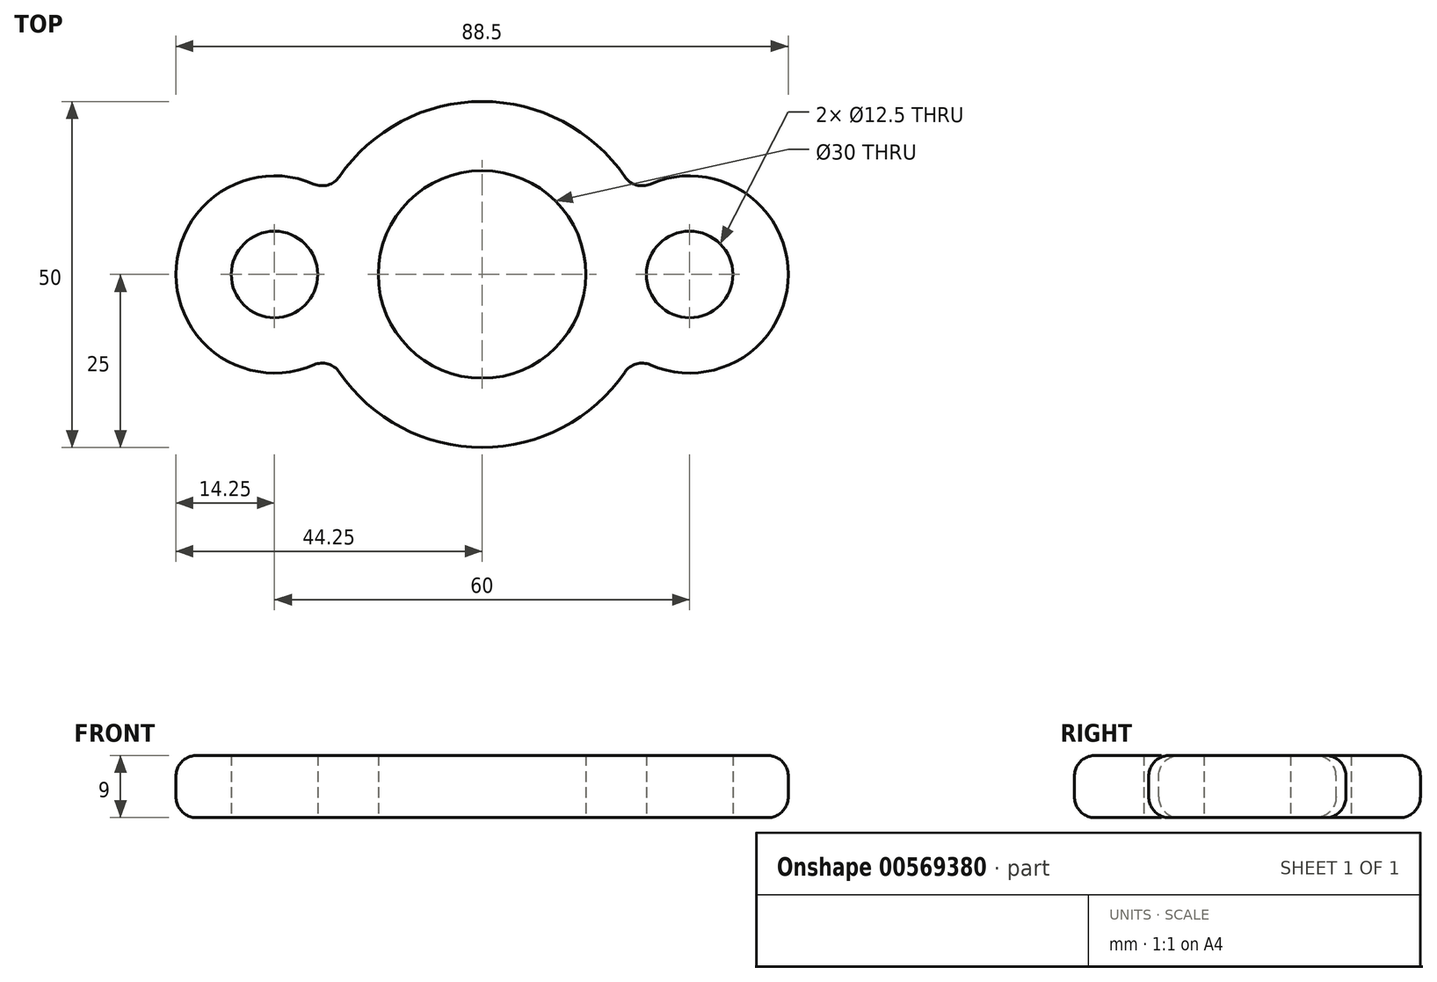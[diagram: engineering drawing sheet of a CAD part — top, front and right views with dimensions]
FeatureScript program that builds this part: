
annotation { "Feature Type Name" : "Feature", "Feature Type Description" : "" }
export const myFeature = defineFeature(function(context is Context, id is Id, definition is map)
    precondition{}
    {
        {
            var Q0;
            Q0=qCreatedBy(makeId("Top.planeOp"),FACE);
            var sketch = newSketch(context, id + "F0", { "sketchPlane" : qUnion([Q0])});
            skCircle(sketch, "E0", {"center": v(0, 0) * mm, "radius": 15 * mm});
            skCircle(sketch, "E1", {"center": v(-30, 0) * mm, "radius": 6.25 * mm});
            skCircle(sketch, "E2", {"center": v(30, 0) * mm, "radius": 6.25 * mm});
            skCircle(sketch, "E3.0", {"center": v(30, 0) * mm, "radius": 14.25 * mm});
            skCircle(sketch, "E4.0", {"center": v(0, 0) * mm, "radius": 25 * mm});
            skCircle(sketch, "E5.0", {"center": v(-30, 0) * mm, "radius": 14.25 * mm});
            skSolve(sketch);
        }
        {
            var Q0;
            {var subQ0=sQuery(id+"F0.wireOp",EDGE,"E4.0");var subQ1=sQuery(id+"F0.wireOp",EDGE,"E1");var subQ2=makeQuery(id+"F0.imprint","INTERSECT",VERTEX,{"disambiguationData":[OD(0.0)],"derivedFrom":[subQ1,subQ0]});Q0=makeQuery(id+"F0.imprint","IMPRINT",FACE,{"disambiguationData":[TD([[makeQuery(id+"F0.imprint","IMPRINT",EDGE,{"disambiguationData":[TD([[subQ2,-1.0]])],"derivedFrom":subQ1}),-1.0]])]});}
            var Q1;
            {var subQ0=sQuery(id+"F0.wireOp",EDGE,"E4.0");var subQ1=sQuery(id+"F0.wireOp",EDGE,"E1");var subQ2=makeQuery(id+"F0.imprint","INTERSECT",VERTEX,{"disambiguationData":[OD(0.0)],"derivedFrom":[subQ1,subQ0]});Q1=makeQuery(id+"F0.imprint","IMPRINT",FACE,{"disambiguationData":[TD([[makeQuery(id+"F0.imprint","IMPRINT",EDGE,{"disambiguationData":[TD([[subQ2,1.0]])],"derivedFrom":subQ1}),-1.0]])]});}
            var Q2;
            Q2=makeQuery(id+"F0.imprint","IMPRINT",FACE,{"disambiguationData":[TD([[makeQuery(id+"F0.imprint","IMPRINT",EDGE,{"derivedFrom":sQuery(id+"F0.wireOp",EDGE,"E0")}),-1.0]])]});
            var Q3;
            {var subQ0=sQuery(id+"F0.wireOp",EDGE,"E4.0");var subQ1=sQuery(id+"F0.wireOp",EDGE,"E2");var subQ2=makeQuery(id+"F0.imprint","INTERSECT",VERTEX,{"disambiguationData":[OD(0.0)],"derivedFrom":[subQ1,subQ0]});Q3=makeQuery(id+"F0.imprint","IMPRINT",FACE,{"disambiguationData":[TD([[makeQuery(id+"F0.imprint","IMPRINT",EDGE,{"disambiguationData":[TD([[subQ2,1.0]])],"derivedFrom":subQ1}),-1.0]])]});}
            var Q4;
            {var subQ0=sQuery(id+"F0.wireOp",EDGE,"E4.0");var subQ1=sQuery(id+"F0.wireOp",EDGE,"E2");var subQ2=makeQuery(id+"F0.imprint","INTERSECT",VERTEX,{"disambiguationData":[OD(0.0)],"derivedFrom":[subQ1,subQ0]});Q4=makeQuery(id+"F0.imprint","IMPRINT",FACE,{"disambiguationData":[TD([[makeQuery(id+"F0.imprint","IMPRINT",EDGE,{"disambiguationData":[TD([[subQ2,-1.0]])],"derivedFrom":subQ1}),-1.0]])]});}
            extrude(context, id + "F1", {"entities" : qUnion([Q0, Q1, Q2, Q3, Q4]), "depth" : 9 * mm, "offsetDistance" : 25 * mm});
        }
        {
            var Q0;
            {var subQ0=sQuery(id+"F0.wireOp",EDGE,"E4.0");Q0=makeQuery(id+"F1.opExtrude","CAP_EDGE",EDGE,{"disambiguationData":[OSD([subQ0]),TDD([makeQuery(id+"F0.imprint","IMPRINT",EDGE,{"disambiguationData":[TD([[makeQuery(id+"F0.imprint","INTERSECT",VERTEX,{"disambiguationData":[OD(1.0)],"derivedFrom":[sQuery(id+"F0.wireOp",EDGE,"E3.0"),subQ0]}),1.0]])],"derivedFrom":subQ0})])],"isStart":true});}
            var Q1;
            {var subQ0=sQuery(id+"F0.wireOp",EDGE,"E4.0");Q1=makeQuery(id+"F1.opExtrude","CAP_EDGE",EDGE,{"disambiguationData":[OSD([subQ0]),TDD([makeQuery(id+"F0.imprint","IMPRINT",EDGE,{"disambiguationData":[TD([[makeQuery(id+"F0.imprint","INTERSECT",VERTEX,{"disambiguationData":[OD(1.0)],"derivedFrom":[sQuery(id+"F0.wireOp",EDGE,"E3.0"),subQ0]}),1.0]])],"derivedFrom":subQ0})])],"isStart":false});}
            var Q2;
            {var subQ0=sQuery(id+"F0.wireOp",EDGE,"E4.0");Q2=makeQuery(id+"F1.opExtrude","CAP_EDGE",EDGE,{"disambiguationData":[OSD([subQ0]),TDD([makeQuery(id+"F0.imprint","IMPRINT",EDGE,{"disambiguationData":[TD([[makeQuery(id+"F0.imprint","INTERSECT",VERTEX,{"disambiguationData":[OD(0.0)],"derivedFrom":[sQuery(id+"F0.wireOp",EDGE,"E3.0"),subQ0]}),-1.0]])],"derivedFrom":subQ0})])],"isStart":true});}
            var Q3;
            {var subQ0=sQuery(id+"F0.wireOp",EDGE,"E4.0");Q3=makeQuery(id+"F1.opExtrude","CAP_EDGE",EDGE,{"disambiguationData":[OSD([subQ0]),TDD([makeQuery(id+"F0.imprint","IMPRINT",EDGE,{"disambiguationData":[TD([[makeQuery(id+"F0.imprint","INTERSECT",VERTEX,{"disambiguationData":[OD(0.0)],"derivedFrom":[sQuery(id+"F0.wireOp",EDGE,"E3.0"),subQ0]}),-1.0]])],"derivedFrom":subQ0})])],"isStart":false});}
            var Q4;
            Q4=makeQuery(id+"F1.opExtrude","CAP_EDGE",EDGE,{"disambiguationData":[OSD([sQuery(id+"F0.wireOp",EDGE,"E5.0")])],"isStart":true});
            var Q5;
            Q5=makeQuery(id+"F1.opExtrude","CAP_EDGE",EDGE,{"disambiguationData":[OSD([sQuery(id+"F0.wireOp",EDGE,"E5.0")])],"isStart":false});
            var Q6;
            Q6=makeQuery(id+"F1.opExtrude","CAP_EDGE",EDGE,{"disambiguationData":[OSD([sQuery(id+"F0.wireOp",EDGE,"E3.0")])],"isStart":true});
            var Q7;
            Q7=makeQuery(id+"F1.opExtrude","CAP_EDGE",EDGE,{"disambiguationData":[OSD([sQuery(id+"F0.wireOp",EDGE,"E3.0")])],"isStart":false});
            var Q8;
            {var subQ0=sQuery(id+"F0.wireOp",EDGE,"E5.0");var subQ1=sQuery(id+"F0.wireOp",EDGE,"E4.0");Q8=makeQuery(id+"F1.opExtrude","SWEPT_EDGE",EDGE,{"disambiguationData":[OSD([subQ1,subQ0]),TDD([makeQuery(id+"F0.imprint","INTERSECT",VERTEX,{"disambiguationData":[OD(1.0)],"derivedFrom":[subQ1,subQ0]})])]});}
            var Q9;
            {var subQ0=sQuery(id+"F0.wireOp",EDGE,"E4.0");var subQ1=sQuery(id+"F0.wireOp",EDGE,"E3.0");Q9=makeQuery(id+"F1.opExtrude","SWEPT_EDGE",EDGE,{"disambiguationData":[OSD([subQ1,subQ0]),TDD([makeQuery(id+"F0.imprint","INTERSECT",VERTEX,{"disambiguationData":[OD(1.0)],"derivedFrom":[subQ1,subQ0]})])]});}
            var Q10;
            {var subQ0=sQuery(id+"F0.wireOp",EDGE,"E5.0");var subQ1=sQuery(id+"F0.wireOp",EDGE,"E4.0");Q10=makeQuery(id+"F1.opExtrude","SWEPT_EDGE",EDGE,{"disambiguationData":[OSD([subQ1,subQ0]),TDD([makeQuery(id+"F0.imprint","INTERSECT",VERTEX,{"disambiguationData":[OD(0.0)],"derivedFrom":[subQ1,subQ0]})])]});}
            var Q11;
            {var subQ0=sQuery(id+"F0.wireOp",EDGE,"E4.0");var subQ1=sQuery(id+"F0.wireOp",EDGE,"E3.0");Q11=makeQuery(id+"F1.opExtrude","SWEPT_EDGE",EDGE,{"disambiguationData":[OSD([subQ1,subQ0]),TDD([makeQuery(id+"F0.imprint","INTERSECT",VERTEX,{"disambiguationData":[OD(0.0)],"derivedFrom":[subQ1,subQ0]})])]});}
            fillet(context, id + "F2", {"entities" : qUnion([Q0, Q1, Q2, Q3, Q4, Q5, Q6, Q7, Q8, Q9, Q10, Q11]), "radius" : 3 * mm, "tangentPropagation" : true, "allowEdgeOverflow" : false});
        }
    });
